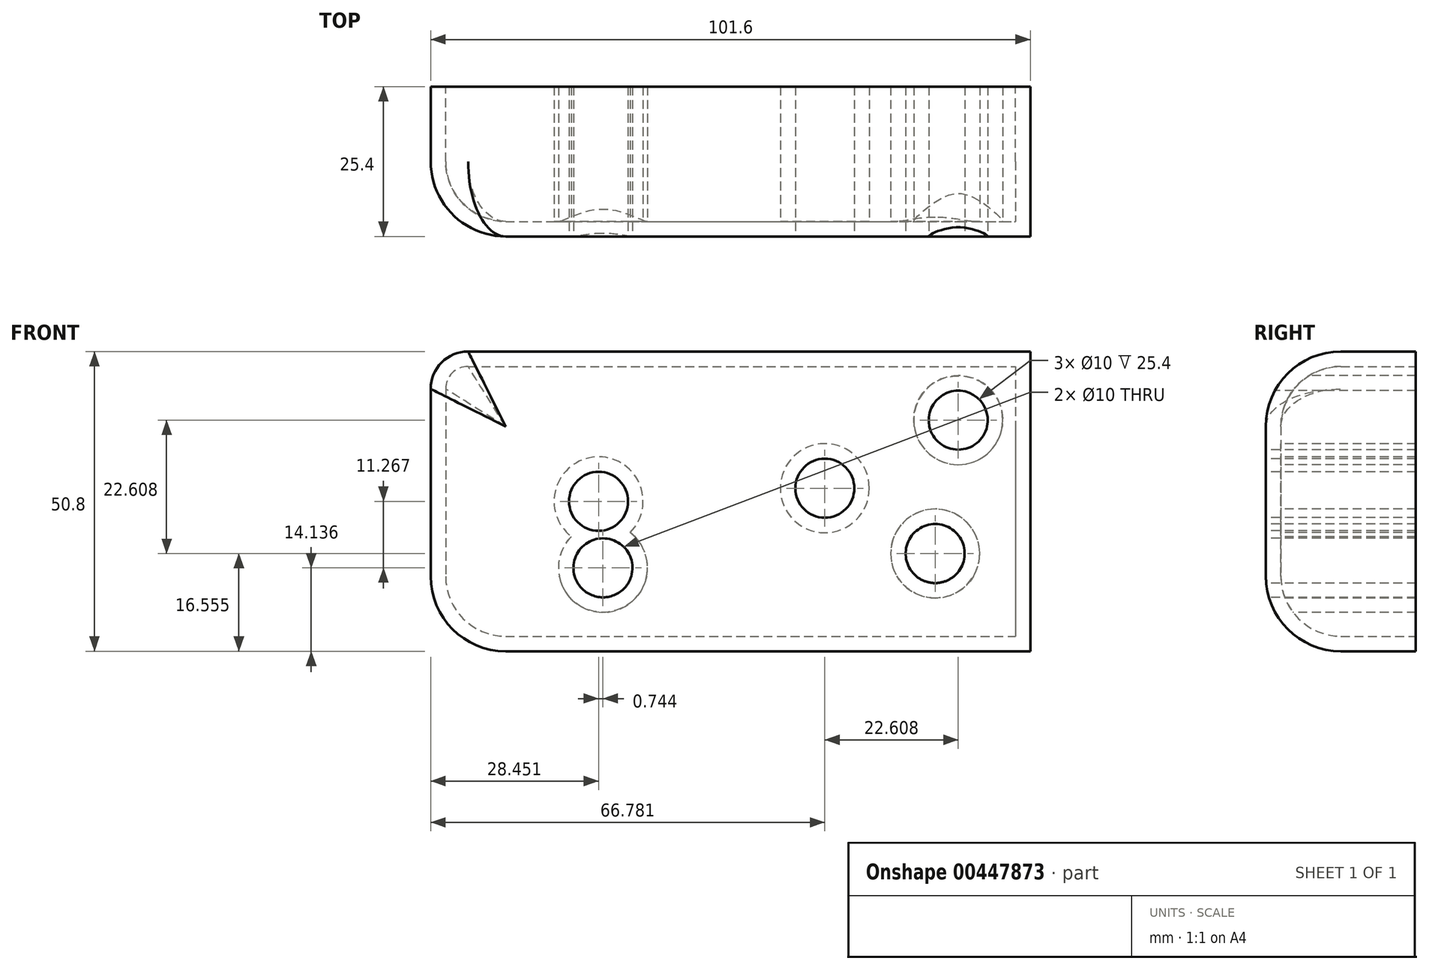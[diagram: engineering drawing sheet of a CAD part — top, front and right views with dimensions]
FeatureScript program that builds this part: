
annotation { "Feature Type Name" : "Feature", "Feature Type Description" : "" }
export const myFeature = defineFeature(function(context is Context, id is Id, definition is map)
    precondition{}
    {
        {
            var Q0;
            Q0=qCreatedBy(makeId("Front.planeOp"),FACE);
            var sketch = newSketch(context, id + "F0", { "sketchPlane" : qUnion([Q0])});
            skLineSegment(sketch, "E0.bottom", {"start": v(-38.9, 12.03) * mm, "end": v(56.36, 12.03) * mm});
            skLineSegment(sketch, "E0.top", {"start": v(-45.24, -38.77) * mm, "end": v(56.36, -38.77) * mm});
            skLineSegment(sketch, "E0.left", {"start": v(-45.24, 5.68) * mm, "end": v(-45.24, -38.77) * mm});
            skLineSegment(sketch, "E0.right", {"start": v(56.36, 12.03) * mm, "end": v(56.36, -38.77) * mm});
            skPoint(sketch, "E1.visualSharp", {"position": v(-45.24, 12.03) * mm});
            skArc(sketch, "E1.filletArc", {"start": v(-38.9, 12.03) * mm, "mid": v(-43.38, 10.17) * mm, "end": v(-45.24, 5.68) * mm});
            skSolve(sketch);
        }
        {
            var Q0;
            Q0 = qSketchRegion(id + "F0", true);
            extrude(context, id + "F1", {"entities" : qUnion([Q0]), "endBound" : BoundingType.SYMMETRIC, "depth" : 25.4 * mm});
        }
        {
            var Q0;
            Q0=makeQuery(id+"F1.opExtrude","CAP_EDGE",EDGE,{"disambiguationData":[OSD([sQuery(id+"F0.wireOp",EDGE,"E0.bottom")])],"isStart":false});
            var Q1;
            Q1=makeQuery(id+"F1.opExtrude","SWEPT_EDGE",EDGE,{"disambiguationData":[OSD([sQuery(id+"F0.wireOp",EDGE,"E0.top"),sQuery(id+"F0.wireOp",EDGE,"E0.left")])]});
            var Q2;
            Q2=makeQuery(id+"F1.opExtrude","CAP_EDGE",EDGE,{"disambiguationData":[OSD([sQuery(id+"F0.wireOp",EDGE,"E0.top")])],"isStart":false});
            fillet(context, id + "F2", {"entities" : qUnion([Q0, Q1, Q2]), "radius" : 12.7 * mm, "tangentPropagation" : true, "allowEdgeOverflow" : false});
        }
        {
            var Q0;
            Q0=makeQuery(id+"F1.opExtrude","CAP_FACE",FACE,{"disambiguationData":[OSD([sQuery(id+"F0.wireOp",EDGE,"E0.bottom"),sQuery(id+"F0.wireOp",EDGE,"E0.top"),sQuery(id+"F0.wireOp",EDGE,"E0.left"),sQuery(id+"F0.wireOp",EDGE,"E0.right"),sQuery(id+"F0.wireOp",EDGE,"E1.filletArc")])],"isStart":false});
            var sketch = newSketch(context, id + "F3", { "sketchPlane" : qUnion([Q0])});
            skPoint(sketch, "E2", {"position": v(-16.79, -13.37) * mm});
            skPoint(sketch, "E3", {"position": v(21.54, -11.14) * mm});
            skPoint(sketch, "E4", {"position": v(-16.05, -24.63) * mm});
            skPoint(sketch, "E5", {"position": v(40.24, -22.22) * mm});
            skPoint(sketch, "E6", {"position": v(44.15, 0.4) * mm});
            skSolve(sketch);
        }
        {
            var Q0;
            Q0=sQuery(id+"F3.wireOp",VERTEX,"E2");
            var Q1;
            Q1=sQuery(id+"F3.wireOp",VERTEX,"E3");
            var Q2;
            Q2=sQuery(id+"F3.wireOp",VERTEX,"E4");
            var Q3;
            Q3=sQuery(id+"F3.wireOp",VERTEX,"E5");
            var Q4;
            Q4=sQuery(id+"F3.wireOp",VERTEX,"E6");
            var Q5;
            Q5=makeQuery(id+"F1.opExtrude","SWEPT_BODY",BODY,{"disambiguationData":[OSD([sQuery(id+"F0.wireOp",EDGE,"E0.bottom"),sQuery(id+"F0.wireOp",EDGE,"E0.top"),sQuery(id+"F0.wireOp",EDGE,"E0.left"),sQuery(id+"F0.wireOp",EDGE,"E0.right"),sQuery(id+"F0.wireOp",EDGE,"E1.filletArc")])]});
            hole(context, id + "F4", {"style" : HoleStyle.SIMPLE, "endStyle" : HoleEndStyle.THROUGH, "holeDiameter" : 10 * mm, "isTappedThrough" : true, "tappedDepth" : 12.7 * mm, "tapClearance" : 3, "locations" : qUnion([Q0, Q1, Q2, Q3, Q4]), "scope" : qUnion([Q5])});
        }
        {
            var Q0;
            Q0=makeQuery(id+"F1.opExtrude","CAP_FACE",FACE,{"disambiguationData":[OSD([sQuery(id+"F0.wireOp",EDGE,"E0.bottom"),sQuery(id+"F0.wireOp",EDGE,"E0.top"),sQuery(id+"F0.wireOp",EDGE,"E0.left"),sQuery(id+"F0.wireOp",EDGE,"E0.right"),sQuery(id+"F0.wireOp",EDGE,"E1.filletArc")])],"isStart":true});
            shell(context, id + "F5", {"entities" : qUnion([Q0]), "thickness" : 2.54 * mm});
        }
    });
